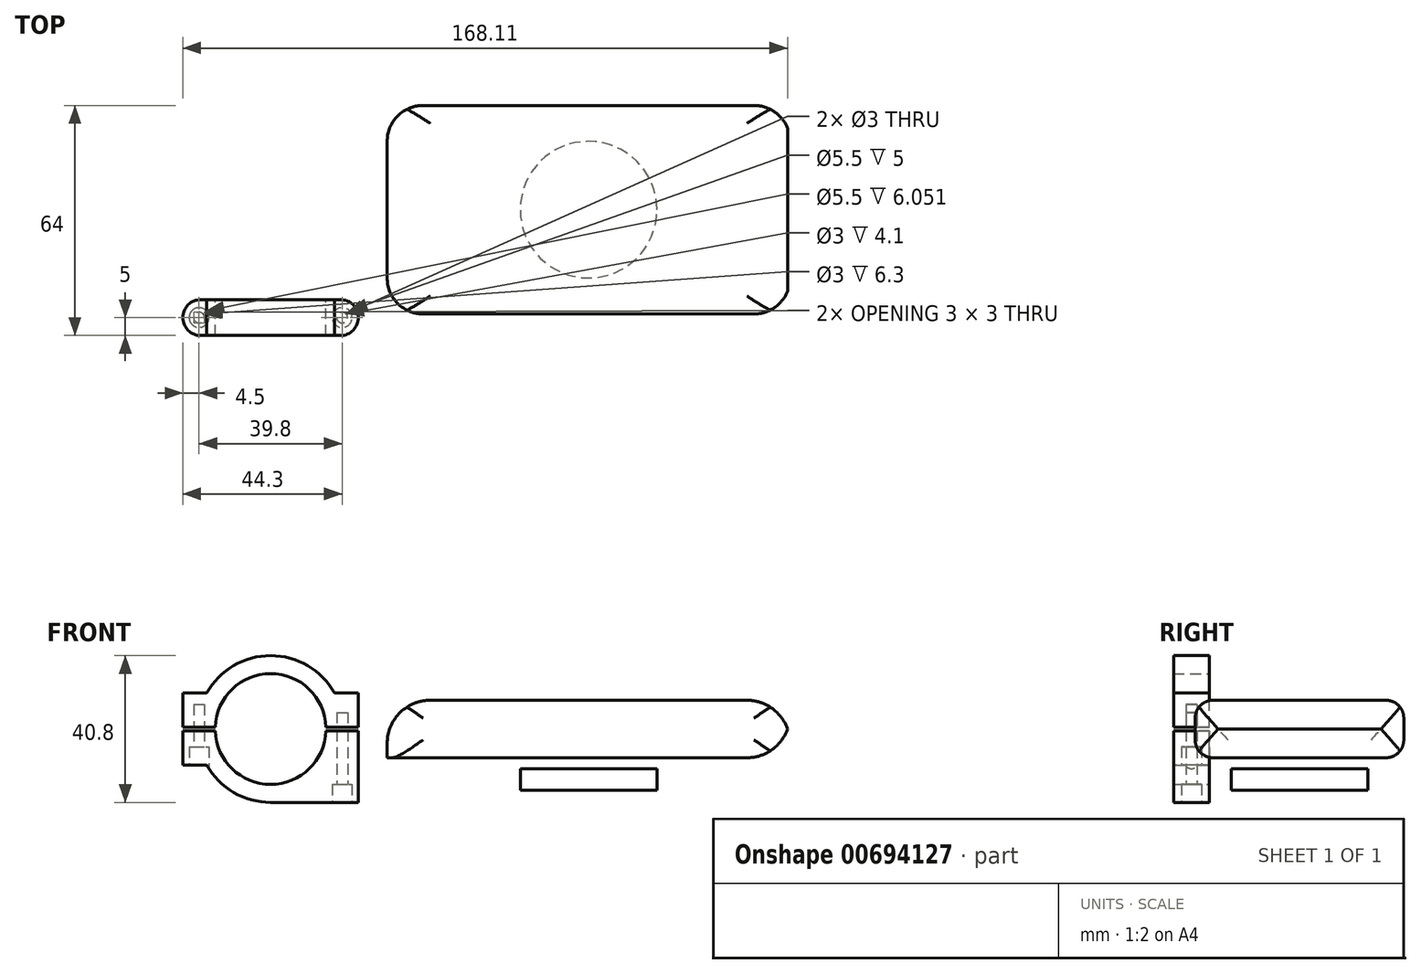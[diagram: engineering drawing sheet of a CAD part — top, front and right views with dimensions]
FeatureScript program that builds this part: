
annotation { "Feature Type Name" : "Feature", "Feature Type Description" : "" }
export const myFeature = defineFeature(function(context is Context, id is Id, definition is map)
    precondition{}
    {
        {
            var Q0;
            Q0=qCreatedBy(makeId("Front.planeOp"),FACE);
            var sketch = newSketch(context, id + "F0", { "sketchPlane" : qUnion([Q0])});
            skCircle(sketch, "E0", {"center": v(0, 0) * mm, "radius": 20.4 * mm});
            skCircle(sketch, "E1", {"center": v(0, 0) * mm, "radius": 15.4 * mm});
            skLineSegment(sketch, "E2.bottom", {"start": v(144.4, -10) * mm, "end": v(32.4, -10) * mm, "construction": true});
            skLineSegment(sketch, "E2.top", {"start": v(144.4, 10) * mm, "end": v(32.4, 10) * mm, "construction": true});
            skLineSegment(sketch, "E2.left", {"start": v(144.4, -10) * mm, "end": v(144.4, 10) * mm, "construction": true});
            skLineSegment(sketch, "E2.right", {"start": v(32.4, -10) * mm, "end": v(32.4, 10) * mm, "construction": true});
            skPoint(sketch, "E2.middle", {"position": v(88.4, 0) * mm});
            skLineSegment(sketch, "E3", {"start": v(21.4, 10) * mm, "end": v(21.4, -20.4) * mm, "construction": true});
            skLineSegment(sketch, "E4.0", {"start": v(18.4, 10) * mm, "end": v(18.4, -20.4) * mm, "construction": true});
            skLineSegment(sketch, "E5", {"start": v(0, -20.4) * mm, "end": v(24.4, -20.4) * mm});
            skLineSegment(sketch, "E6", {"start": v(24.4, -20.4) * mm, "end": v(24.4, 10) * mm});
            skLineSegment(sketch, "E7", {"start": v(24.4, 10) * mm, "end": v(17.78, 10) * mm});
            skLineSegment(sketch, "E8.MirrorCS", {"start": v(-24.4, 10) * mm, "end": v(-17.78, 10) * mm});
            skLineSegment(sketch, "E9.MirrorCS", {"start": v(-24.4, -10) * mm, "end": v(-24.4, 10) * mm});
            skLineSegment(sketch, "E10", {"start": v(-24.4, 0) * mm, "end": v(24.4, 0) * mm, "construction": true});
            skLineSegment(sketch, "E11.0", {"start": v(-24.4, -0.5) * mm, "end": v(24.4, -0.5) * mm});
            skLineSegment(sketch, "E12.0", {"start": v(-24.4, 0.5) * mm, "end": v(24.4, 0.5) * mm});
            skLineSegment(sketch, "E13", {"start": v(-18.4, 10) * mm, "end": v(-18.4, -10) * mm, "construction": true});
            skLineSegment(sketch, "E14.0", {"start": v(-21.4, 10) * mm, "end": v(-21.4, -10) * mm, "construction": true});
            skLineSegment(sketch, "E15", {"start": v(-24.4, -10) * mm, "end": v(-17.78, -10) * mm});
            skPoint(sketch, "E16.orphan", {"position": v(0, -20.4) * mm});
            skPoint(sketch, "E17.MirrorCS.end.orphan", {"position": v(-24.4, -20.4) * mm});
            skSolve(sketch);
        }
        {
            var Q0;
            {var subQ4=sQuery(id+"F0.wireOp",EDGE,"E0");var subQ7=makeQuery(id+"F0.imprint","INTERSECT",VERTEX,{"derivedFrom":[subQ4,sQuery(id+"F0.wireOp",EDGE,"E7")]});Q0=makeQuery(id+"F0.imprint","IMPRINT",FACE,{"disambiguationData":[TD([[makeQuery(id+"F0.imprint","IMPRINT",EDGE,{"disambiguationData":[TD([[subQ7,1.0]])],"derivedFrom":subQ4}),1.0]])]});}
            var Q1;
            {var subQ0=sQuery(id+"F0.wireOp",EDGE,"E11.0");var subQ3=sQuery(id+"F0.wireOp",EDGE,"E1");var subQ4=makeQuery(id+"F0.imprint","INTERSECT",VERTEX,{"disambiguationData":[OD(0.0)],"derivedFrom":[subQ3,subQ0]});Q1=makeQuery(id+"F0.imprint","IMPRINT",FACE,{"disambiguationData":[TD([[makeQuery(id+"F0.imprint","IMPRINT",EDGE,{"disambiguationData":[TD([[subQ4,-1.0]])],"derivedFrom":subQ3}),-1.0]])]});}
            var Q2;
            {var subQ0=sQuery(id+"F0.wireOp",EDGE,"E7");Q2=makeQuery(id+"F0.imprint","IMPRINT",FACE,{"disambiguationData":[TD([[makeQuery(id+"F0.imprint","IMPRINT",EDGE,{"derivedFrom":subQ0}),1.0]])]});}
            var Q3;
            {var subQ0=sQuery(id+"F0.wireOp",EDGE,"E5");Q3=makeQuery(id+"F0.imprint","IMPRINT",FACE,{"disambiguationData":[TD([[makeQuery(id+"F0.imprint","IMPRINT",EDGE,{"derivedFrom":subQ0}),1.0]])]});}
            var Q4;
            {var subQ0=sQuery(id+"F0.wireOp",EDGE,"E17.MirrorCS");Q4=makeQuery(id+"F0.imprint","IMPRINT",FACE,{"disambiguationData":[TD([[makeQuery(id+"F0.imprint","IMPRINT",EDGE,{"derivedFrom":subQ0}),-1.0]])]});}
            var Q5;
            {var subQ0=sQuery(id+"F0.wireOp",EDGE,"E8.MirrorCS");Q5=makeQuery(id+"F0.imprint","IMPRINT",FACE,{"disambiguationData":[TD([[makeQuery(id+"F0.imprint","IMPRINT",EDGE,{"derivedFrom":subQ0}),-1.0]])]});}
            var Q6;
            {var subQ0=sQuery(id+"F0.wireOp",EDGE,"E15");Q6=makeQuery(id+"F0.imprint","IMPRINT",FACE,{"disambiguationData":[TD([[makeQuery(id+"F0.imprint","IMPRINT",EDGE,{"derivedFrom":subQ0}),1.0]])]});}
            extrude(context, id + "F1", {"entities" : qUnion([Q0, Q1, Q2, Q3, Q4, Q5, Q6]), "endBound" : BoundingType.SYMMETRIC, "depth" : 10 * mm, "offsetDistance" : 25 * mm});
        }
        {
            var Q0;
            Q0=makeQuery(id+"F1.opExtrude","SWEPT_FACE",FACE,{"disambiguationData":[OSD([sQuery(id+"F0.wireOp",EDGE,"E5")])]});
            var sketch = newSketch(context, id + "F2", { "sketchPlane" : qUnion([Q0])});
            skCircle(sketch, "E18", {"center": v(19.9, 0) * mm, "radius": 1.5 * mm});
            skSolve(sketch);
        }
        {
            var Q0;
            Q0 = qSketchRegion(id + "F2", true);
            extrude(context, id + "F3", {"entities" : qUnion([Q0]), "operationType" : NewBodyOperationType.REMOVE, "oppositeDirection" : true, "depth" : 25 * mm, "offsetDistance" : 25 * mm});
        }
        {
            var Q0;
            Q0=makeQuery(id+"F1.opExtrude","SWEPT_FACE",FACE,{"disambiguationData":[OSD([sQuery(id+"F0.wireOp",EDGE,"E5"),sQuery(id+"F0.wireOp",EDGE,"E17.MirrorCS")])]});
            var sketch = newSketch(context, id + "F4", { "sketchPlane" : qUnion([Q0])});
            skCircle(sketch, "E19", {"center": v(19.9, 0) * mm, "radius": 2.75 * mm});
            skSolve(sketch);
        }
        {
            var Q0;
            Q0=makeQuery(id+"F4.imprint","IMPRINT",FACE,{"disambiguationData":[TD([[makeQuery(id+"F4.imprint","IMPRINT",EDGE,{"derivedFrom":sQuery(id+"F4.wireOp",EDGE,"E19")}),1.0]])]});
            extrude(context, id + "F5", {"entities" : qUnion([Q0]), "operationType" : NewBodyOperationType.REMOVE, "oppositeDirection" : true, "depth" : 5 * mm, "offsetDistance" : 25 * mm});
        }
        {
            var Q0;
            {var subQ0=sQuery(id+"F0.wireOp",EDGE,"E9.MirrorCS");Q0=makeQuery(id+"F1.opExtrude","CAP_EDGE",EDGE,{"disambiguationData":[OSD([subQ0]),TDD([makeQuery(id+"F0.imprint","IMPRINT",EDGE,{"disambiguationData":[TD([[makeQuery(id+"F0.imprint","INTERSECT",VERTEX,{"derivedFrom":[subQ0,sQuery(id+"F0.wireOp",EDGE,"E15")]}),-1.0]])],"derivedFrom":subQ0})])],"isStart":false});}
            var Q1;
            {var subQ0=sQuery(id+"F0.wireOp",EDGE,"E9.MirrorCS");Q1=makeQuery(id+"F1.opExtrude","CAP_EDGE",EDGE,{"disambiguationData":[OSD([subQ0]),TDD([makeQuery(id+"F0.imprint","IMPRINT",EDGE,{"disambiguationData":[TD([[makeQuery(id+"F0.imprint","INTERSECT",VERTEX,{"derivedFrom":[subQ0,sQuery(id+"F0.wireOp",EDGE,"E15")]}),-1.0]])],"derivedFrom":subQ0})])],"isStart":true});}
            var Q2;
            {var subQ0=sQuery(id+"F0.wireOp",EDGE,"E9.MirrorCS");Q2=makeQuery(id+"F1.opExtrude","CAP_EDGE",EDGE,{"disambiguationData":[OSD([subQ0]),TDD([makeQuery(id+"F0.imprint","IMPRINT",EDGE,{"disambiguationData":[TD([[makeQuery(id+"F0.imprint","INTERSECT",VERTEX,{"derivedFrom":[sQuery(id+"F0.wireOp",EDGE,"E8.MirrorCS"),subQ0]}),1.0]])],"derivedFrom":subQ0})])],"isStart":false});}
            var Q3;
            {var subQ0=sQuery(id+"F0.wireOp",EDGE,"E9.MirrorCS");Q3=makeQuery(id+"F1.opExtrude","CAP_EDGE",EDGE,{"disambiguationData":[OSD([subQ0]),TDD([makeQuery(id+"F0.imprint","IMPRINT",EDGE,{"disambiguationData":[TD([[makeQuery(id+"F0.imprint","INTERSECT",VERTEX,{"derivedFrom":[sQuery(id+"F0.wireOp",EDGE,"E8.MirrorCS"),subQ0]}),1.0]])],"derivedFrom":subQ0})])],"isStart":true});}
            var Q4;
            {var subQ0=sQuery(id+"F0.wireOp",EDGE,"E6");Q4=makeQuery(id+"F1.opExtrude","CAP_EDGE",EDGE,{"disambiguationData":[OSD([subQ0]),TDD([makeQuery(id+"F0.imprint","IMPRINT",EDGE,{"disambiguationData":[TD([[makeQuery(id+"F0.imprint","INTERSECT",VERTEX,{"derivedFrom":[subQ0,sQuery(id+"F0.wireOp",EDGE,"E7")]}),1.0]])],"derivedFrom":subQ0})])],"isStart":false});}
            var Q5;
            {var subQ0=sQuery(id+"F0.wireOp",EDGE,"E6");Q5=makeQuery(id+"F1.opExtrude","CAP_EDGE",EDGE,{"disambiguationData":[OSD([subQ0]),TDD([makeQuery(id+"F0.imprint","IMPRINT",EDGE,{"disambiguationData":[TD([[makeQuery(id+"F0.imprint","INTERSECT",VERTEX,{"derivedFrom":[subQ0,sQuery(id+"F0.wireOp",EDGE,"E7")]}),1.0]])],"derivedFrom":subQ0})])],"isStart":true});}
            var Q6;
            {var subQ0=sQuery(id+"F0.wireOp",EDGE,"E6");Q6=makeQuery(id+"F1.opExtrude","CAP_EDGE",EDGE,{"disambiguationData":[OSD([subQ0]),TDD([makeQuery(id+"F0.imprint","IMPRINT",EDGE,{"disambiguationData":[TD([[makeQuery(id+"F0.imprint","INTERSECT",VERTEX,{"derivedFrom":[sQuery(id+"F0.wireOp",EDGE,"E5"),subQ0]}),-1.0]])],"derivedFrom":subQ0})])],"isStart":false});}
            var Q7;
            {var subQ0=sQuery(id+"F0.wireOp",EDGE,"E6");Q7=makeQuery(id+"F1.opExtrude","CAP_EDGE",EDGE,{"disambiguationData":[OSD([subQ0]),TDD([makeQuery(id+"F0.imprint","IMPRINT",EDGE,{"disambiguationData":[TD([[makeQuery(id+"F0.imprint","INTERSECT",VERTEX,{"derivedFrom":[sQuery(id+"F0.wireOp",EDGE,"E5"),subQ0]}),-1.0]])],"derivedFrom":subQ0})])],"isStart":true});}
            fillet(context, id + "F6", {"entities" : qUnion([Q0, Q1, Q2, Q3, Q4, Q5, Q6, Q7]), "radius" : 5 * mm, "tangentPropagation" : true, "allowEdgeOverflow" : false});
        }
        {
            var Q0;
            Q0=makeQuery(id+"F1.opExtrude","SWEPT_FACE",FACE,{"disambiguationData":[OSD([sQuery(id+"F0.wireOp",EDGE,"E15")])]});
            var sketch = newSketch(context, id + "F7", { "sketchPlane" : qUnion([Q0])});
            skCircle(sketch, "E20", {"center": v(-19.9, 0) * mm, "radius": 1.5 * mm});
            skPoint(sketch, "E20.centerSnap0", {"position": v(-17.78, 0) * mm});
            skSolve(sketch);
        }
        {
            var Q0;
            Q0=makeQuery(id+"F7.imprint","IMPRINT",FACE,{"disambiguationData":[TD([[makeQuery(id+"F7.imprint","IMPRINT",EDGE,{"derivedFrom":sQuery(id+"F7.wireOp",EDGE,"E20")}),1.0]])]});
            extrude(context, id + "F8", {"entities" : qUnion([Q0]), "operationType" : NewBodyOperationType.REMOVE, "oppositeDirection" : true, "depth" : 16.8 * mm, "offsetDistance" : 25 * mm});
        }
        {
            var Q0;
            Q0=makeQuery(id+"F1.opExtrude","SWEPT_FACE",FACE,{"disambiguationData":[OSD([sQuery(id+"F0.wireOp",EDGE,"E15")])]});
            var sketch = newSketch(context, id + "F9", { "sketchPlane" : qUnion([Q0])});
            skCircle(sketch, "E21", {"center": v(-19.9, 0) * mm, "radius": 2.75 * mm});
            skSolve(sketch);
        }
        {
            var Q0;
            Q0 = qSketchRegion(id + "F9", true);
            extrude(context, id + "F10", {"entities" : qUnion([Q0]), "operationType" : NewBodyOperationType.REMOVE, "oppositeDirection" : true, "depth" : 5 * mm, "offsetDistance" : 25 * mm, "hasSecondDirection" : true, "secondDirectionOppositeDirection" : false, "secondDirectionDepth" : 10.6 * mm});
        }
        {
            var Q0;
            Q0=qCreatedBy(makeId("Top.planeOp"),FACE);
            var sketch = newSketch(context, id + "F11", { "sketchPlane" : qUnion([Q0])});
            skLineSegment(sketch, "E22.bottom", {"start": v(134.4, 1) * mm, "end": v(42.4, 1) * mm});
            skLineSegment(sketch, "E22.top", {"start": v(134.4, 59) * mm, "end": v(42.4, 59) * mm});
            skLineSegment(sketch, "E22.left", {"start": v(144.4, 11) * mm, "end": v(144.4, 49) * mm});
            skLineSegment(sketch, "E22.right", {"start": v(32.4, 11) * mm, "end": v(32.4, 49) * mm});
            skPoint(sketch, "E22.middle", {"position": v(88.4, 30) * mm});
            skCircle(sketch, "E23", {"center": v(88.4, 30) * mm, "radius": 66 * mm, "construction": true});
            skPoint(sketch, "E24.visualSharp", {"position": v(32.4, 59) * mm});
            skArc(sketch, "E24.filletArc", {"start": v(42.4, 59) * mm, "mid": v(35.33, 56.07) * mm, "end": v(32.4, 49) * mm});
            skPoint(sketch, "E25.visualSharp", {"position": v(32.4, 1) * mm});
            skArc(sketch, "E25.filletArc", {"start": v(32.4, 11) * mm, "mid": v(35.33, 3.93) * mm, "end": v(42.4, 1) * mm});
            skPoint(sketch, "E26.visualSharp", {"position": v(144.4, 1) * mm});
            skArc(sketch, "E26.filletArc", {"start": v(134.4, 1) * mm, "mid": v(141.47, 3.93) * mm, "end": v(144.4, 11) * mm});
            skPoint(sketch, "E27.visualSharp", {"position": v(144.4, 59) * mm});
            skArc(sketch, "E27.filletArc", {"start": v(144.4, 49) * mm, "mid": v(141.47, 56.07) * mm, "end": v(134.4, 59) * mm});
            skSolve(sketch);
        }
        {
            var Q0;
            Q0=makeQuery(id+"F11.imprint","IMPRINT",FACE,{"disambiguationData":[TD([[makeQuery(id+"F11.imprint","IMPRINT",EDGE,{"derivedFrom":sQuery(id+"F11.wireOp",EDGE,"E22.bottom")}),-1.0]])]});
            extrude(context, id + "F12", {"entities" : qUnion([Q0]), "endBound" : BoundingType.SYMMETRIC, "depth" : 16 * mm, "offsetDistance" : 25 * mm});
        }
        {
            var Q0;
            Q0=makeQuery(id+"F12.opExtrude","CAP_EDGE",EDGE,{"disambiguationData":[OSD([sQuery(id+"F11.wireOp",EDGE,"E22.bottom")])],"isStart":false});
            var Q1;
            Q1=makeQuery(id+"F12.opExtrude","CAP_EDGE",EDGE,{"disambiguationData":[OSD([sQuery(id+"F11.wireOp",EDGE,"E22.top")])],"isStart":false});
            var Q2;
            Q2=makeQuery(id+"F12.opExtrude","CAP_EDGE",EDGE,{"disambiguationData":[OSD([sQuery(id+"F11.wireOp",EDGE,"E22.bottom")])],"isStart":true});
            var Q3;
            Q3=makeQuery(id+"F12.opExtrude","CAP_EDGE",EDGE,{"disambiguationData":[OSD([sQuery(id+"F11.wireOp",EDGE,"E22.top")])],"isStart":true});
            fillet(context, id + "F13", {"entities" : qUnion([Q0, Q1, Q2, Q3]), "radius" : 5 * mm, "allowEdgeOverflow" : false});
        }
        {
            var Q0;
            Q0=makeQuery(id+"F12.opExtrude","CAP_EDGE",EDGE,{"disambiguationData":[OSD([sQuery(id+"F11.wireOp",EDGE,"E22.left")])],"isStart":false});
            var Q1;
            Q1=makeQuery(id+"F12.opExtrude","CAP_EDGE",EDGE,{"disambiguationData":[OSD([sQuery(id+"F11.wireOp",EDGE,"E22.right")])],"isStart":false});
            var Q2;
            Q2=makeQuery(id+"F12.opExtrude","CAP_EDGE",EDGE,{"disambiguationData":[OSD([sQuery(id+"F11.wireOp",EDGE,"E22.left")])],"isStart":true});
            fillet(context, id + "F14", {"entities" : qUnion([Q0, Q1, Q2]), "radius" : 12 * mm, "allowEdgeOverflow" : false});
        }
        {
            var Q0;
            Q0=makeQuery(id+"F12.opExtrude","CAP_FACE",FACE,{"disambiguationData":[OSD([sQuery(id+"F11.wireOp",EDGE,"E22.bottom"),sQuery(id+"F11.wireOp",EDGE,"E22.top"),sQuery(id+"F11.wireOp",EDGE,"E22.left"),sQuery(id+"F11.wireOp",EDGE,"E22.right"),sQuery(id+"F11.wireOp",EDGE,"E24.filletArc"),sQuery(id+"F11.wireOp",EDGE,"E25.filletArc"),sQuery(id+"F11.wireOp",EDGE,"E26.filletArc"),sQuery(id+"F11.wireOp",EDGE,"E27.filletArc")])],"isStart":true});
            cPlane(context, id + "F15", {"entities" : qUnion([Q0]), "cplaneType" : CPlaneType.OFFSET, "offset" : 3 * mm, "width" : 150 * mm, "height" : 150 * mm});
        }
        {
            var Q0;
            Q0=qCreatedBy(id+"F15.planeOp",FACE);
            var sketch = newSketch(context, id + "F16", { "sketchPlane" : qUnion([Q0])});
            skCircle(sketch, "E28", {"center": v(88.4, -30) * mm, "radius": 19 * mm});
            skSolve(sketch);
        }
        {
            var Q0;
            Q0 = qSketchRegion(id + "F16", true);
            extrude(context, id + "F17", {"entities" : qUnion([Q0]), "depth" : 6 * mm, "offsetDistance" : 25 * mm});
        }
    });
